annotation { "Feature Type Name" : "Feature", "Feature Type Description" : "" }
export const myFeature = defineFeature(function(context is Context, id is Id, definition is map)
    precondition{}
    {
        {
            var Q0;
            Q0=qCreatedBy(makeId("Top.planeOp"),FACE);
            var sketch = newSketch(context, id + "F0", { "sketchPlane" : qUnion([Q0])});
            skLineSegment(sketch, "E0", {"start": v(-39, 120) * mm, "end": v(39, 120) * mm, "construction": true});
            skLineSegment(sketch, "E1", {"start": v(41, 120) * mm, "end": v(41, 22) * mm, "construction": true});
            skLineSegment(sketch, "E2", {"start": v(39, 22) * mm, "end": v(35, 22) * mm});
            skLineSegment(sketch, "E3", {"start": v(35, -22) * mm, "end": v(39, -22) * mm});
            skLineSegment(sketch, "E4", {"start": v(41, -24) * mm, "end": v(41, -118) * mm});
            skLineSegment(sketch, "E5", {"start": v(39, -120) * mm, "end": v(-39, -120) * mm});
            skLineSegment(sketch, "E6", {"start": v(-41, -118) * mm, "end": v(-41, 92.5) * mm});
            skLineSegment(sketch, "E7", {"start": v(33, -20) * mm, "end": v(33, 20) * mm});
            skPoint(sketch, "E8", {"position": v(0, 120) * mm});
            skPoint(sketch, "E9", {"position": v(33, 0) * mm});
            skCircle(sketch, "E10", {"center": v(-20, 78) * mm, "radius": 13.25 * mm});
            skCircle(sketch, "E11.0.1.0", {"center": v(-20, 48) * mm, "radius": 13.25 * mm});
            skCircle(sketch, "E11.0.2.0", {"center": v(-20, 18) * mm, "radius": 13.25 * mm});
            skCircle(sketch, "E11.0.3.0", {"center": v(-20, -12) * mm, "radius": 13.25 * mm});
            skCircle(sketch, "E11.0.4.0", {"center": v(-20, -42) * mm, "radius": 13.25 * mm});
            skCircle(sketch, "E11.0.5.0", {"center": v(-20, -72) * mm, "radius": 13.25 * mm});
            skCircle(sketch, "E11.0.6.0", {"center": v(-20, -102) * mm, "radius": 13.25 * mm});
            skCircle(sketch, "E11.1.0.0", {"center": v(12, 78) * mm, "radius": 13.25 * mm});
            skCircle(sketch, "E11.1.1.0", {"center": v(12, 48) * mm, "radius": 13.25 * mm});
            skCircle(sketch, "E11.1.2.0", {"center": v(12, 18) * mm, "radius": 13.25 * mm});
            skCircle(sketch, "E11.1.3.0", {"center": v(12, -12) * mm, "radius": 13.25 * mm});
            skCircle(sketch, "E11.1.4.0", {"center": v(12, -42) * mm, "radius": 13.25 * mm});
            skCircle(sketch, "E11.1.5.0", {"center": v(12, -72) * mm, "radius": 13.25 * mm});
            skCircle(sketch, "E11.1.6.0", {"center": v(12, -102) * mm, "radius": 13.25 * mm});
            skLineSegment(sketch, "E11.direction1", {"start": v(-20, 78) * mm, "end": v(12, 78) * mm, "construction": true});
            skLineSegment(sketch, "E11.direction2", {"start": v(-20, 78) * mm, "end": v(-20, 48) * mm, "construction": true});
            skLineSegment(sketch, "E12.bottom", {"start": v(-32, 115.5) * mm, "end": v(39, 115.5) * mm, "construction": true});
            skLineSegment(sketch, "E12.top", {"start": v(-39, 94.5) * mm, "end": v(39, 94.5) * mm});
            skLineSegment(sketch, "E12.left", {"start": v(-34, 113.5) * mm, "end": v(-34, 96.5) * mm, "construction": true});
            skLineSegment(sketch, "E12.right", {"start": v(41, 115.5) * mm, "end": v(41, 94.5) * mm, "construction": true});
            skLineSegment(sketch, "E13", {"start": v(41, 118) * mm, "end": v(41, 117.5) * mm, "construction": true});
            skLineSegment(sketch, "E14", {"start": v(41, 92.5) * mm, "end": v(41, 72) * mm});
            skLineSegment(sketch, "E15", {"start": v(41, 72) * mm, "end": v(39, 72) * mm});
            skLineSegment(sketch, "E16", {"start": v(39, 72) * mm, "end": v(39, 60) * mm});
            skLineSegment(sketch, "E17", {"start": v(39, 60) * mm, "end": v(41, 60) * mm});
            skLineSegment(sketch, "E18", {"start": v(41, 60) * mm, "end": v(41, 24) * mm});
            skPoint(sketch, "E19.visualSharp", {"position": v(-41, 120) * mm});
            skPoint(sketch, "E20.visualSharp", {"position": v(41, 120) * mm});
            skArc(sketch, "E20.filletArc", {"start": v(41, 118) * mm, "mid": v(40.41, 119.41) * mm, "end": v(39, 120) * mm, "construction": true});
            skPoint(sketch, "E21.visualSharp", {"position": v(41, 115.5) * mm});
            skArc(sketch, "E21.filletArc", {"start": v(39, 115.5) * mm, "mid": v(40.41, 116.09) * mm, "end": v(41, 117.5) * mm, "construction": true});
            skPoint(sketch, "E22.visualSharp", {"position": v(41, 94.5) * mm});
            skArc(sketch, "E22.filletArc", {"start": v(41, 92.5) * mm, "mid": v(40.41, 93.91) * mm, "end": v(39, 94.5) * mm});
            skPoint(sketch, "E23.visualSharp", {"position": v(-34, 115.5) * mm});
            skArc(sketch, "E23.filletArc", {"start": v(-32, 115.5) * mm, "mid": v(-33.41, 114.91) * mm, "end": v(-34, 113.5) * mm, "construction": true});
            skPoint(sketch, "E24.visualSharp", {"position": v(-34, 94.5) * mm});
            skPoint(sketch, "E25.visualSharp", {"position": v(41, 22) * mm});
            skArc(sketch, "E25.filletArc", {"start": v(39, 22) * mm, "mid": v(40.41, 22.59) * mm, "end": v(41, 24) * mm});
            skPoint(sketch, "E26.visualSharp", {"position": v(33, 22) * mm});
            skArc(sketch, "E26.filletArc", {"start": v(35, 22) * mm, "mid": v(33.59, 21.41) * mm, "end": v(33, 20) * mm});
            skPoint(sketch, "E27.visualSharp", {"position": v(33, -22) * mm});
            skArc(sketch, "E27.filletArc", {"start": v(33, -20) * mm, "mid": v(33.59, -21.41) * mm, "end": v(35, -22) * mm});
            skPoint(sketch, "E28.visualSharp", {"position": v(41, -22) * mm});
            skArc(sketch, "E28.filletArc", {"start": v(41, -24) * mm, "mid": v(40.41, -22.59) * mm, "end": v(39, -22) * mm});
            skPoint(sketch, "E29.visualSharp", {"position": v(41, -120) * mm});
            skArc(sketch, "E29.filletArc", {"start": v(39, -120) * mm, "mid": v(40.41, -119.41) * mm, "end": v(41, -118) * mm});
            skPoint(sketch, "E30.visualSharp", {"position": v(-41, -120) * mm});
            skArc(sketch, "E30.filletArc", {"start": v(-41, -118) * mm, "mid": v(-40.41, -119.41) * mm, "end": v(-39, -120) * mm});
            skText(sketch, "E31", { "text": "Digital Toolbox", "fontName": "OpenSans-Regular.ttf"});
            skPoint(sketch, "E32.visualSharp", {"position": v(-41, 94.5) * mm});
            skArc(sketch, "E32.filletArc", {"start": v(-39, 94.5) * mm, "mid": v(-40.41, 93.91) * mm, "end": v(-41, 92.5) * mm});
            const initialGuessF0  = {"E31": [0.02916, -0.0308, 0, -1, 0.008]};
            skSetInitialGuess(sketch, initialGuessF0);
            skSolve(sketch);
        }
        {
            var Q0;
            Q0 = qSketchRegion(id + "F0", true);
            extrude(context, id + "F1", {"entities" : qUnion([Q0]), "depth" : 1.2 * mm});
        }
    });